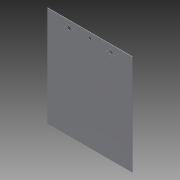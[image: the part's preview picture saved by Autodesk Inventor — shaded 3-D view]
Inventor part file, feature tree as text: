
AUTODESK INVENTOR PART (.ipt)
format: ipt  version: 2014 SP1 (Build 180222100, 222)  size: 118,784 bytes
history: native  units: mm
features: extrude x1, sketch x1
ambient origin geometry x8: Origin, YZ Plane, XZ Plane, XY Plane, X Axis, Y Axis, Z Axis, Center Point
bodies: Body1 (feature_tree)
feature tree (2):
  extrude  "Extrusion5"  Depth=360.0mm
  sketch  "Sketch9"  dims[d22=304.8mm d23=360.0mm d24=19.0mm d25=10.0mm d27=12.0mm d28=12.0mm d30=28.0mm d31=4.0mm d32=4.0mm d33=4.0mm d34=4.0mm d35=75.0mm d36=11.0mm d37=77.4mm d38=25.0mm d39=28.0mm d40=4.0mm d41=4.0mm d42=4.0mm d43=4.0mm d44=11.0mm d45=1.5875mm d46=0.0mm]
